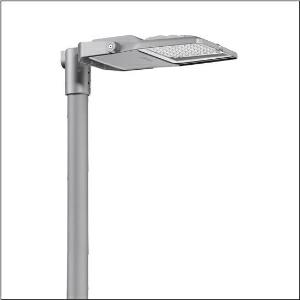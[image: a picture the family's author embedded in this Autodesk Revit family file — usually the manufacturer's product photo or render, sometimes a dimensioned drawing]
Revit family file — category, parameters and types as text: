
# Revit family: floodlight_fl_21_mini___pl52_5xa7776c2d3a_1d2c
name_source: partatom
category: Lighting Fixtures
units: mm (PartAtom-declared; Revit-internal decimal feet)

## family parameters
Cut with Voids When Loaded = No
Host = Face
Light Source = No
Part Type = Normal
Room Calculation Point = No
Round Connector Dimension = Use Diameter
Shared = No

## types (1)
- --- (1 x LED, 12190 lm, 89 W, 3000K)
    Apparent Load = 89 VA
    CIE Flux Codes = 26 60 98 100 100
    Color Rendering = 70
    Color Temperature = 3000K
    Default Elevation = 1800 mm
    Description = Floodlight FL 21 mini, floodlight, primary light control with lens, of PMMA, primary optical cover: protective disc, of toughened safety glass, transparent, light distribution: PL52, light emission: direct distribution, installation type: surface-mounted, LED, High Power LED, rated luminous flux: 12.190lm, luminous efficacy: 137lm/W, light colour: 730, colour temperature: 3000K, control: flexible luminous flux parameterisation, time-dependent luminous flux control, constant luminous flux control, overheat protection, presetting dimming logarithmic, with terminal, 6-pole, mains connection: 220..240V, AC, 50/60Hz, start of lifetime: 89W, end of service life: 94W, reduction: 43W, luminaire housing, of diecast aluminium, powder-coated, Siteco® metallic grey (DB 702S), corrosivity category C5 mid according to DIN EN ISO 12944, sealing non-destructively replaceable, please order mast flange separately, mast bracket, of steel, galvanised, powder-coated, Siteco® metallic grey (DB 702S), Smart Interface below and above, protection rating (complete): IP66, insulation class (complete): insulation class II (safety insulation), certification: CE, ENEC, VDE, protection symbol: D, impact resistance: IK08, permissible operating ambient temperature: -40..+40°C, permissible operating ambient temperature for outdoor applications: -40..+50°C, standard: DIN EN 12944, LABS conformity tested according to VDMA 24364:2018-05, packaging unit: 1 piece

Light Distribution: PL52
    Height = 70 mm
    Lamp = 1 x LED
    Lamp Light Flux = 12190 lm
    Lamp Power = 89 W
    Lamp count = 1
    Length = 485 mm
    Luminous efficacy = 137 lm/W
    Manufacturer = Siteco
    ModVariant = No
    Model = 5XA7776C2D3A
    Number of Poles = 1
    OnlyDefault = Yes
    Power Factor = 1
    Product Name = Floodlight FL 21 mini | PL52
    Product group = floodlight | pylon annexe
    ProductGroupID = 6200
    Protection Class = Protection class II
    Protection Degree = IP 66
    RLX_Detail_Level = 1
    RLX_Emergency_Light_Flux = 0 lm
    RLX_Emergency_Type = 0
    RLX_Emergency_Type_DB = No
    RlxData = <blob elided: 101025 chars, md5=3653f00e>
    Socket = socket
    Standby Power = 0 W
    System Light Flux = 12190 lm
    System Power = 89 W
    Type Comments = factory setting: luminous flux: 100 % | dim-lin: 254 | 456 mA
    Type Image = l_1007125.jpg
    URL = http://relux.com
    VarID = @adj_113409
    Voltage = 0 V
    Weight = 0.00 kg
    Width = 337 mm

## geometry (parser evidence)
native form markers: Blend x4, Sweep x11
no freeform markers — native parametric forms only
